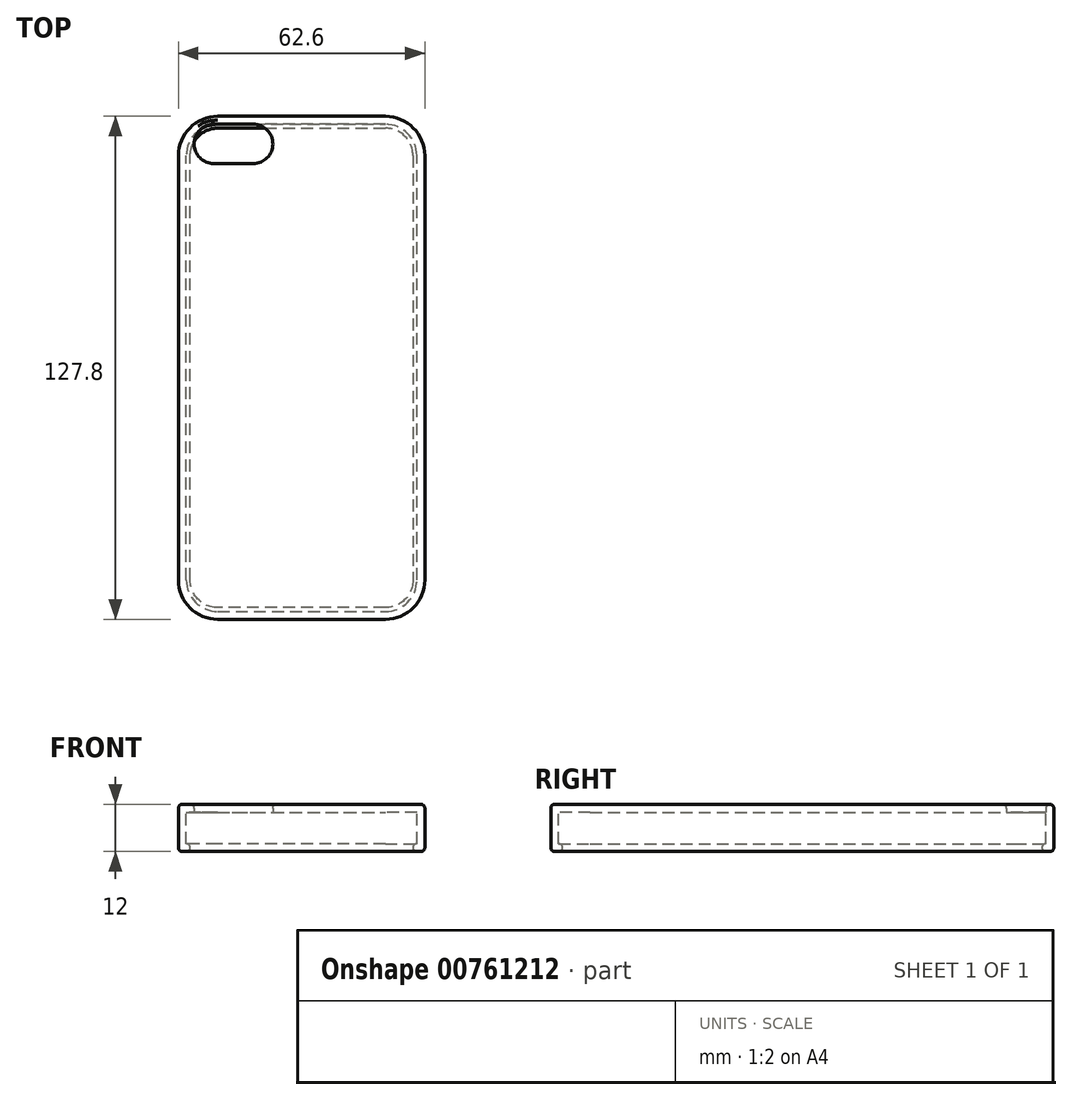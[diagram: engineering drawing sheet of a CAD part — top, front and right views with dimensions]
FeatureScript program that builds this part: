
annotation { "Feature Type Name" : "Feature", "Feature Type Description" : "" }
export const myFeature = defineFeature(function(context is Context, id is Id, definition is map)
    precondition{}
    {
        {
            var Q0;
            Q0=qCreatedBy(makeId("Top.planeOp"),FACE);
            var sketch = newSketch(context, id + "F0", { "sketchPlane" : qUnion([Q0])});
            skLineSegment(sketch, "E0.bottom", {"start": v(10, 0) * mm, "end": v(52.6, 0) * mm});
            skLineSegment(sketch, "E0.top", {"start": v(10, 127.8) * mm, "end": v(52.6, 127.8) * mm});
            skLineSegment(sketch, "E0.left", {"start": v(0, 10) * mm, "end": v(0, 117.8) * mm});
            skLineSegment(sketch, "E0.right", {"start": v(62.6, 10) * mm, "end": v(62.6, 117.8) * mm});
            skPoint(sketch, "E1.visualSharp", {"position": v(0, 127.8) * mm});
            skArc(sketch, "E1.filletArc", {"start": v(10, 127.8) * mm, "mid": v(2.93, 124.87) * mm, "end": v(0, 117.8) * mm});
            skPoint(sketch, "E2.visualSharp", {"position": v(62.6, 127.8) * mm});
            skArc(sketch, "E2.filletArc", {"start": v(62.6, 117.8) * mm, "mid": v(59.67, 124.87) * mm, "end": v(52.6, 127.8) * mm});
            skPoint(sketch, "E3.visualSharp", {"position": v(62.6, 0) * mm});
            skArc(sketch, "E3.filletArc", {"start": v(52.6, 0) * mm, "mid": v(59.67, 2.93) * mm, "end": v(62.6, 10) * mm});
            skPoint(sketch, "E4.visualSharp", {"position": v(0, 0) * mm});
            skArc(sketch, "E4.filletArc", {"start": v(0, 10) * mm, "mid": v(2.93, 2.93) * mm, "end": v(10, 0) * mm});
            skLineSegment(sketch, "E5.bottom", {"start": v(9, 125.8) * mm, "end": v(19, 125.8) * mm});
            skLineSegment(sketch, "E5.top", {"start": v(9, 115.8) * mm, "end": v(19, 115.8) * mm});
            skLineSegment(sketch, "E5.left", {"start": v(4, 120.8) * mm, "end": v(4, 120.8) * mm});
            skLineSegment(sketch, "E5.right", {"start": v(24, 120.8) * mm, "end": v(24, 120.8) * mm});
            skPoint(sketch, "E6.visualSharp", {"position": v(4, 125.8) * mm});
            skArc(sketch, "E6.filletArc", {"start": v(9, 125.8) * mm, "mid": v(5.46, 124.34) * mm, "end": v(4, 120.8) * mm});
            skPoint(sketch, "E7.visualSharp", {"position": v(4, 115.8) * mm});
            skArc(sketch, "E7.filletArc", {"start": v(4, 120.8) * mm, "mid": v(5.46, 117.26) * mm, "end": v(9, 115.8) * mm});
            skPoint(sketch, "E8.visualSharp", {"position": v(24, 115.8) * mm});
            skArc(sketch, "E8.filletArc", {"start": v(19, 115.8) * mm, "mid": v(22.54, 117.26) * mm, "end": v(24, 120.8) * mm});
            skPoint(sketch, "E9.visualSharp", {"position": v(24, 125.8) * mm});
            skArc(sketch, "E9.filletArc", {"start": v(24, 120.8) * mm, "mid": v(22.54, 124.34) * mm, "end": v(19, 125.8) * mm});
            skSolve(sketch);
        }
        {
            var Q0;
            Q0 = qSketchRegion(id + "F0", true);
            extrude(context, id + "F1", {"entities" : qUnion([Q0]), "depth" : 2 * mm, "offsetDistance" : 25 * mm});
        }
        {
            var Q0;
            Q0=qCreatedBy(makeId("Top.planeOp"),FACE);
            var sketch = newSketch(context, id + "F2", { "sketchPlane" : qUnion([Q0])});
            skLineSegment(sketch, "E10.bottom", {"start": v(10, 0) * mm, "end": v(52.6, 0) * mm});
            skLineSegment(sketch, "E10.top", {"start": v(10, 127.8) * mm, "end": v(52.6, 127.8) * mm});
            skLineSegment(sketch, "E10.left", {"start": v(0, 10) * mm, "end": v(0, 117.8) * mm});
            skLineSegment(sketch, "E10.right", {"start": v(62.6, 10) * mm, "end": v(62.6, 117.8) * mm});
            skPoint(sketch, "E11.visualSharp", {"position": v(0, 127.8) * mm});
            skArc(sketch, "E11.filletArc", {"start": v(10, 127.8) * mm, "mid": v(2.93, 124.87) * mm, "end": v(0, 117.8) * mm});
            skPoint(sketch, "E12.visualSharp", {"position": v(62.6, 127.8) * mm});
            skArc(sketch, "E12.filletArc", {"start": v(62.6, 117.8) * mm, "mid": v(59.67, 124.87) * mm, "end": v(52.6, 127.8) * mm});
            skPoint(sketch, "E13.visualSharp", {"position": v(62.6, 0) * mm});
            skArc(sketch, "E13.filletArc", {"start": v(52.6, 0) * mm, "mid": v(59.67, 2.93) * mm, "end": v(62.6, 10) * mm});
            skPoint(sketch, "E14.visualSharp", {"position": v(0, 0) * mm});
            skArc(sketch, "E14.filletArc", {"start": v(0, 10) * mm, "mid": v(2.93, 2.93) * mm, "end": v(10, 0) * mm});
            skLineSegment(sketch, "E15.left", {"start": v(-67.03, 59.16) * mm, "end": v(-67.03, 59.16) * mm});
            skLineSegment(sketch, "E15.right", {"start": v(-47.03, 59.16) * mm, "end": v(-47.03, 59.16) * mm});
            skArc(sketch, "E16.0", {"start": v(2, 10) * mm, "mid": v(4.34, 4.34) * mm, "end": v(10, 2) * mm});
            skLineSegment(sketch, "E16.1", {"start": v(2, 10) * mm, "end": v(2, 117.8) * mm});
            skLineSegment(sketch, "E16.2", {"start": v(10, 2) * mm, "end": v(52.6, 2) * mm});
            skArc(sketch, "E16.3", {"start": v(10, 125.8) * mm, "mid": v(4.34, 123.46) * mm, "end": v(2, 117.8) * mm});
            skArc(sketch, "E16.4", {"start": v(52.6, 2) * mm, "mid": v(58.26, 4.34) * mm, "end": v(60.6, 10) * mm});
            skLineSegment(sketch, "E16.5", {"start": v(60.6, 10) * mm, "end": v(60.6, 117.8) * mm});
            skArc(sketch, "E16.6", {"start": v(60.6, 117.8) * mm, "mid": v(58.26, 123.46) * mm, "end": v(52.6, 125.8) * mm});
            skLineSegment(sketch, "E16.7", {"start": v(10, 125.8) * mm, "end": v(52.6, 125.8) * mm});
            skSolve(sketch);
        }
        {
            var Q0;
            Q0 = qSketchRegion(id + "F2", true);
            extrude(context, id + "F3", {"entities" : qUnion([Q0]), "operationType" : NewBodyOperationType.ADD, "oppositeDirection" : true, "depth" : 10 * mm, "offsetDistance" : 25 * mm});
        }
        {
            var Q0;
            Q0=makeQuery(id+"F3.opExtrude","CAP_FACE",FACE,{"disambiguationData":[OSD([sQuery(id+"F2.wireOp",EDGE,"E10.bottom"),sQuery(id+"F2.wireOp",EDGE,"E10.top"),sQuery(id+"F2.wireOp",EDGE,"E10.left"),sQuery(id+"F2.wireOp",EDGE,"E10.right"),sQuery(id+"F2.wireOp",EDGE,"E11.filletArc"),sQuery(id+"F2.wireOp",EDGE,"E12.filletArc"),sQuery(id+"F2.wireOp",EDGE,"E13.filletArc"),sQuery(id+"F2.wireOp",EDGE,"E14.filletArc"),sQuery(id+"F2.wireOp",EDGE,"E16.0"),sQuery(id+"F2.wireOp",EDGE,"E16.1"),sQuery(id+"F2.wireOp",EDGE,"E16.2"),sQuery(id+"F2.wireOp",EDGE,"E16.3"),sQuery(id+"F2.wireOp",EDGE,"E16.4"),sQuery(id+"F2.wireOp",EDGE,"E16.5"),sQuery(id+"F2.wireOp",EDGE,"E16.6"),sQuery(id+"F2.wireOp",EDGE,"E16.7")])],"isStart":false});
            var sketch = newSketch(context, id + "F4", { "sketchPlane" : qUnion([Q0])});
            skLineSegment(sketch, "E17.bottom", {"start": v(10, -127.8) * mm, "end": v(52.6, -127.8) * mm});
            skLineSegment(sketch, "E17.top", {"start": v(10, 0) * mm, "end": v(52.6, 0) * mm});
            skLineSegment(sketch, "E17.left", {"start": v(0, -117.8) * mm, "end": v(0, -10) * mm});
            skLineSegment(sketch, "E17.right", {"start": v(62.6, -117.8) * mm, "end": v(62.6, -10) * mm});
            skPoint(sketch, "E18.visualSharp", {"position": v(0, 0) * mm});
            skArc(sketch, "E18.filletArc", {"start": v(10, 0) * mm, "mid": v(2.93, -2.93) * mm, "end": v(0, -10) * mm});
            skPoint(sketch, "E19.visualSharp", {"position": v(62.6, 0) * mm});
            skArc(sketch, "E19.filletArc", {"start": v(62.6, -10) * mm, "mid": v(59.67, -2.93) * mm, "end": v(52.6, 0) * mm});
            skPoint(sketch, "E20.visualSharp", {"position": v(62.6, -127.8) * mm});
            skArc(sketch, "E20.filletArc", {"start": v(52.6, -127.8) * mm, "mid": v(59.67, -124.87) * mm, "end": v(62.6, -117.8) * mm});
            skPoint(sketch, "E21.visualSharp", {"position": v(0, -127.8) * mm});
            skArc(sketch, "E21.filletArc", {"start": v(0, -117.8) * mm, "mid": v(2.93, -124.87) * mm, "end": v(10, -127.8) * mm});
            skLineSegment(sketch, "E22.left", {"start": v(-230.7, 16.2) * mm, "end": v(-230.7, 16.2) * mm});
            skLineSegment(sketch, "E22.right", {"start": v(-210.7, 16.2) * mm, "end": v(-210.7, 16.2) * mm});
            skArc(sketch, "E23.0", {"start": v(3, -117.8) * mm, "mid": v(5.05, -122.75) * mm, "end": v(10, -124.8) * mm});
            skLineSegment(sketch, "E23.1", {"start": v(3, -117.8) * mm, "end": v(3, -10) * mm});
            skLineSegment(sketch, "E23.2", {"start": v(10, -124.8) * mm, "end": v(52.6, -124.8) * mm});
            skArc(sketch, "E23.3", {"start": v(10, -3) * mm, "mid": v(5.05, -5.05) * mm, "end": v(3, -10) * mm});
            skArc(sketch, "E23.4", {"start": v(52.6, -124.8) * mm, "mid": v(57.55, -122.75) * mm, "end": v(59.6, -117.8) * mm});
            skLineSegment(sketch, "E23.5", {"start": v(59.6, -117.8) * mm, "end": v(59.6, -10) * mm});
            skArc(sketch, "E23.6", {"start": v(59.6, -10) * mm, "mid": v(57.55, -5.05) * mm, "end": v(52.6, -3) * mm});
            skLineSegment(sketch, "E23.7", {"start": v(10, -3) * mm, "end": v(52.6, -3) * mm});
            skSolve(sketch);
        }
        {
            var Q0;
            Q0 = qSketchRegion(id + "F4", true);
            extrude(context, id + "F5", {"entities" : qUnion([Q0]), "operationType" : NewBodyOperationType.ADD, "oppositeDirection" : true, "depth" : 2 * mm, "offsetDistance" : 25 * mm});
        }
        {
            var Q0;
            Q0=makeQuery(id+"F5.opExtrude","CAP_EDGE",EDGE,{"disambiguationData":[OSD([sQuery(id+"F4.wireOp",EDGE,"E23.2")])],"isStart":true});
            fillet(context, id + "F6", {"entities" : qUnion([Q0]), "radius" : 1 * mm, "tangentPropagation" : true, "allowEdgeOverflow" : false});
        }
        {
            var Q0;
            Q0=makeQuery(id+"F5.opExtrude","CAP_EDGE",EDGE,{"disambiguationData":[OSD([sQuery(id+"F4.wireOp",EDGE,"E23.2")])],"isStart":false});
            var Q1;
            Q1=makeQuery(id+"F5.opExtrude","CAP_EDGE",EDGE,{"disambiguationData":[OSD([sQuery(id+"F4.wireOp",EDGE,"E23.4")])],"isStart":false});
            var Q2;
            Q2=makeQuery(id+"F5.opExtrude","CAP_EDGE",EDGE,{"disambiguationData":[OSD([sQuery(id+"F4.wireOp",EDGE,"E23.5")])],"isStart":false});
            var Q3;
            Q3=makeQuery(id+"F5.opExtrude","CAP_EDGE",EDGE,{"disambiguationData":[OSD([sQuery(id+"F4.wireOp",EDGE,"E23.6")])],"isStart":false});
            var Q4;
            Q4=makeQuery(id+"F5.opExtrude","CAP_EDGE",EDGE,{"disambiguationData":[OSD([sQuery(id+"F4.wireOp",EDGE,"E23.7")])],"isStart":false});
            var Q5;
            Q5=makeQuery(id+"F5.opExtrude","CAP_EDGE",EDGE,{"disambiguationData":[OSD([sQuery(id+"F4.wireOp",EDGE,"E23.3")])],"isStart":false});
            var Q6;
            Q6=makeQuery(id+"F5.opExtrude","CAP_EDGE",EDGE,{"disambiguationData":[OSD([sQuery(id+"F4.wireOp",EDGE,"E23.1")])],"isStart":false});
            var Q7;
            Q7=makeQuery(id+"F5.opExtrude","CAP_EDGE",EDGE,{"disambiguationData":[OSD([sQuery(id+"F4.wireOp",EDGE,"E23.0")])],"isStart":false});
            fillet(context, id + "F7", {"entities" : qUnion([Q0, Q1, Q2, Q3, Q4, Q5, Q6, Q7]), "radius" : 1 * mm, "tangentPropagation" : true, "allowEdgeOverflow" : false});
        }
        {
            var Q0;
            Q0=makeQuery(id+"F3.opExtrude","CAP_EDGE",EDGE,{"disambiguationData":[OSD([sQuery(id+"F2.wireOp",EDGE,"E10.right")])],"isStart":false});
            var Q1;
            Q1=makeQuery(id+"F3.opExtrude","CAP_EDGE",EDGE,{"disambiguationData":[OSD([sQuery(id+"F2.wireOp",EDGE,"E12.filletArc")])],"isStart":false});
            var Q2;
            Q2=makeQuery(id+"F3.opExtrude","CAP_EDGE",EDGE,{"disambiguationData":[OSD([sQuery(id+"F2.wireOp",EDGE,"E10.top")])],"isStart":false});
            var Q3;
            Q3=makeQuery(id+"F3.opExtrude","CAP_EDGE",EDGE,{"disambiguationData":[OSD([sQuery(id+"F2.wireOp",EDGE,"E11.filletArc")])],"isStart":false});
            var Q4;
            Q4=makeQuery(id+"F3.opExtrude","CAP_EDGE",EDGE,{"disambiguationData":[OSD([sQuery(id+"F2.wireOp",EDGE,"E10.left")])],"isStart":false});
            var Q5;
            Q5=makeQuery(id+"F3.opExtrude","CAP_EDGE",EDGE,{"disambiguationData":[OSD([sQuery(id+"F2.wireOp",EDGE,"E14.filletArc")])],"isStart":false});
            var Q6;
            Q6=makeQuery(id+"F3.opExtrude","CAP_EDGE",EDGE,{"disambiguationData":[OSD([sQuery(id+"F2.wireOp",EDGE,"E10.bottom")])],"isStart":false});
            var Q7;
            Q7=makeQuery(id+"F3.opExtrude","CAP_EDGE",EDGE,{"disambiguationData":[OSD([sQuery(id+"F2.wireOp",EDGE,"E13.filletArc")])],"isStart":false});
            fillet(context, id + "F8", {"entities" : qUnion([Q0, Q1, Q2, Q3, Q4, Q5, Q6, Q7]), "radius" : 1 * mm, "tangentPropagation" : true, "allowEdgeOverflow" : false});
        }
        {
            var Q0;
            Q0=makeQuery(id+"F1.opExtrude","CAP_EDGE",EDGE,{"disambiguationData":[OSD([sQuery(id+"F0.wireOp",EDGE,"E0.bottom")])],"isStart":false});
            var Q1;
            Q1=makeQuery(id+"F1.opExtrude","CAP_EDGE",EDGE,{"disambiguationData":[OSD([sQuery(id+"F0.wireOp",EDGE,"E4.filletArc")])],"isStart":false});
            var Q2;
            Q2=makeQuery(id+"F1.opExtrude","CAP_FACE",FACE,{"disambiguationData":[OSD([sQuery(id+"F0.wireOp",EDGE,"E0.bottom"),sQuery(id+"F0.wireOp",EDGE,"E0.top"),sQuery(id+"F0.wireOp",EDGE,"E0.left"),sQuery(id+"F0.wireOp",EDGE,"E0.right"),sQuery(id+"F0.wireOp",EDGE,"E1.filletArc"),sQuery(id+"F0.wireOp",EDGE,"E2.filletArc"),sQuery(id+"F0.wireOp",EDGE,"E3.filletArc"),sQuery(id+"F0.wireOp",EDGE,"E4.filletArc"),sQuery(id+"F0.wireOp",EDGE,"E5.bottom"),sQuery(id+"F0.wireOp",EDGE,"E5.top"),sQuery(id+"F0.wireOp",EDGE,"E6.filletArc"),sQuery(id+"F0.wireOp",EDGE,"E7.filletArc"),sQuery(id+"F0.wireOp",EDGE,"E8.filletArc"),sQuery(id+"F0.wireOp",EDGE,"E9.filletArc")])],"isStart":false});
            fillet(context, id + "F9", {"entities" : qUnion([Q0, Q1, Q2]), "radius" : 1 * mm, "tangentPropagation" : true, "allowEdgeOverflow" : false});
        }
    });
